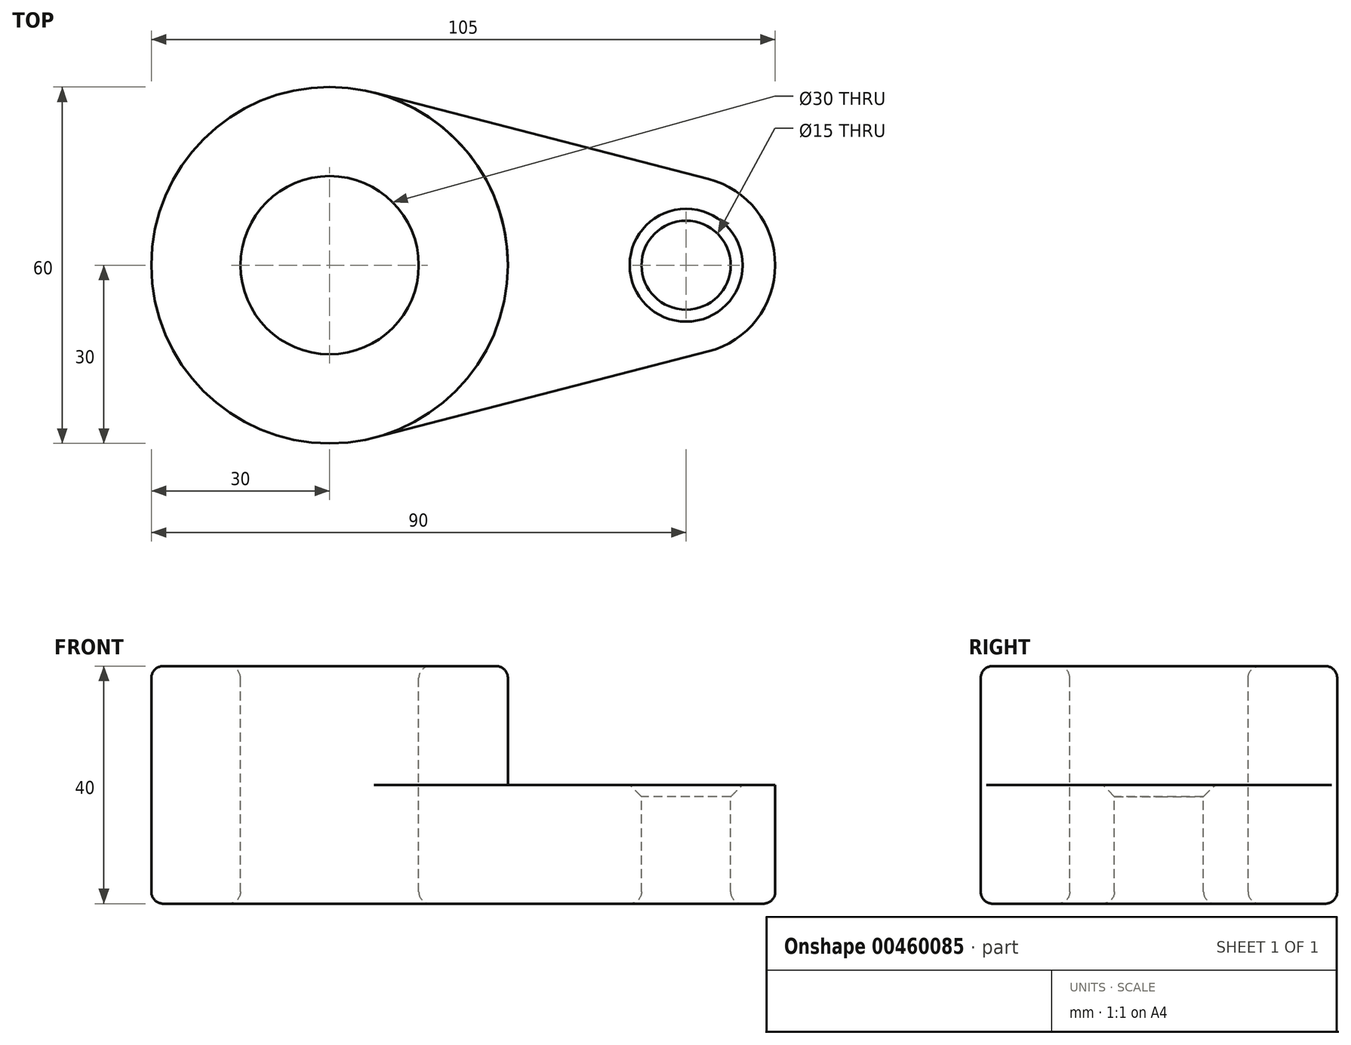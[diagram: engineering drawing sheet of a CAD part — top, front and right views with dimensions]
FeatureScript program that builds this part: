
annotation { "Feature Type Name" : "Feature", "Feature Type Description" : "" }
export const myFeature = defineFeature(function(context is Context, id is Id, definition is map)
    precondition{}
    {
        {
            var Q0;
            Q0=qCreatedBy(makeId("Top.planeOp"),FACE);
            var sketch = newSketch(context, id + "F0", { "sketchPlane" : qUnion([Q0])});
            skCircle(sketch, "E0", {"center": v(0, 0) * mm, "radius": 30 * mm});
            skCircle(sketch, "E1", {"center": v(60, 0) * mm, "radius": 15 * mm});
            skLineSegment(sketch, "E2", {"start": v(7.5, 29.05) * mm, "end": v(63.75, 14.52) * mm});
            skLineSegment(sketch, "E3.MirrorCS", {"start": v(7.5, -29.05) * mm, "end": v(63.75, -14.52) * mm});
            skCircle(sketch, "E4", {"center": v(0, 0) * mm, "radius": 15 * mm});
            skCircle(sketch, "E5", {"center": v(60, 0) * mm, "radius": 7.5 * mm});
            skSolve(sketch);
        }
        {
            var Q0;
            Q0=makeQuery(id+"F0.imprint","IMPRINT",FACE,{"disambiguationData":[TD([[makeQuery(id+"F0.imprint","IMPRINT",EDGE,{"derivedFrom":sQuery(id+"F0.wireOp",EDGE,"E4")}),-1.0]])]});
            var Q1;
            {var subQ0=sQuery(id+"F0.wireOp",EDGE,"E2");Q1=makeQuery(id+"F0.imprint","IMPRINT",FACE,{"disambiguationData":[TD([[makeQuery(id+"F0.imprint","IMPRINT",EDGE,{"derivedFrom":subQ0}),-1.0]])]});}
            var Q2;
            Q2=makeQuery(id+"F0.imprint","IMPRINT",FACE,{"disambiguationData":[TD([[makeQuery(id+"F0.imprint","IMPRINT",EDGE,{"derivedFrom":sQuery(id+"F0.wireOp",EDGE,"E5")}),-1.0]])]});
            extrude(context, id + "F1", {"entities" : qUnion([Q0, Q1, Q2]), "oppositeDirection" : true, "depth" : 20 * mm});
        }
        {
            var Q0;
            Q0=makeQuery(id+"F0.imprint","IMPRINT",FACE,{"disambiguationData":[TD([[makeQuery(id+"F0.imprint","IMPRINT",EDGE,{"derivedFrom":sQuery(id+"F0.wireOp",EDGE,"E4")}),-1.0]])]});
            extrude(context, id + "F2", {"entities" : qUnion([Q0]), "operationType" : NewBodyOperationType.ADD, "depth" : 20 * mm});
        }
        {
            var Q0;
            Q0=makeQuery(id+"F2.opExtrude","CAP_EDGE",EDGE,{"disambiguationData":[OSD([sQuery(id+"F0.wireOp",EDGE,"E0")])],"isStart":false});
            var Q1;
            Q1=makeQuery(id+"F2.opExtrude","CAP_EDGE",EDGE,{"disambiguationData":[OSD([sQuery(id+"F0.wireOp",EDGE,"E4")])],"isStart":false});
            var Q2;
            Q2=makeQuery(id+"F1.opExtrude","CAP_FACE",FACE,{"disambiguationData":[OSD([sQuery(id+"F0.wireOp",EDGE,"E0"),sQuery(id+"F0.wireOp",EDGE,"E1"),sQuery(id+"F0.wireOp",EDGE,"E2"),sQuery(id+"F0.wireOp",EDGE,"E3.MirrorCS"),sQuery(id+"F0.wireOp",EDGE,"E4"),sQuery(id+"F0.wireOp",EDGE,"E5")])],"isStart":false});
            fillet(context, id + "F3", {"entities" : qUnion([Q0, Q1, Q2]), "radius" : 2 * mm, "tangentPropagation" : true, "allowEdgeOverflow" : false});
        }
        {
            var Q0;
            Q0=makeQuery(id+"F1.opExtrude","CAP_EDGE",EDGE,{"disambiguationData":[OSD([sQuery(id+"F0.wireOp",EDGE,"E5")])],"isStart":true});
            chamfer(context, id + "F4", {"entities" : qUnion([Q0]), "width" : 2 * mm, "tangentPropagation" : true});
        }
    });
